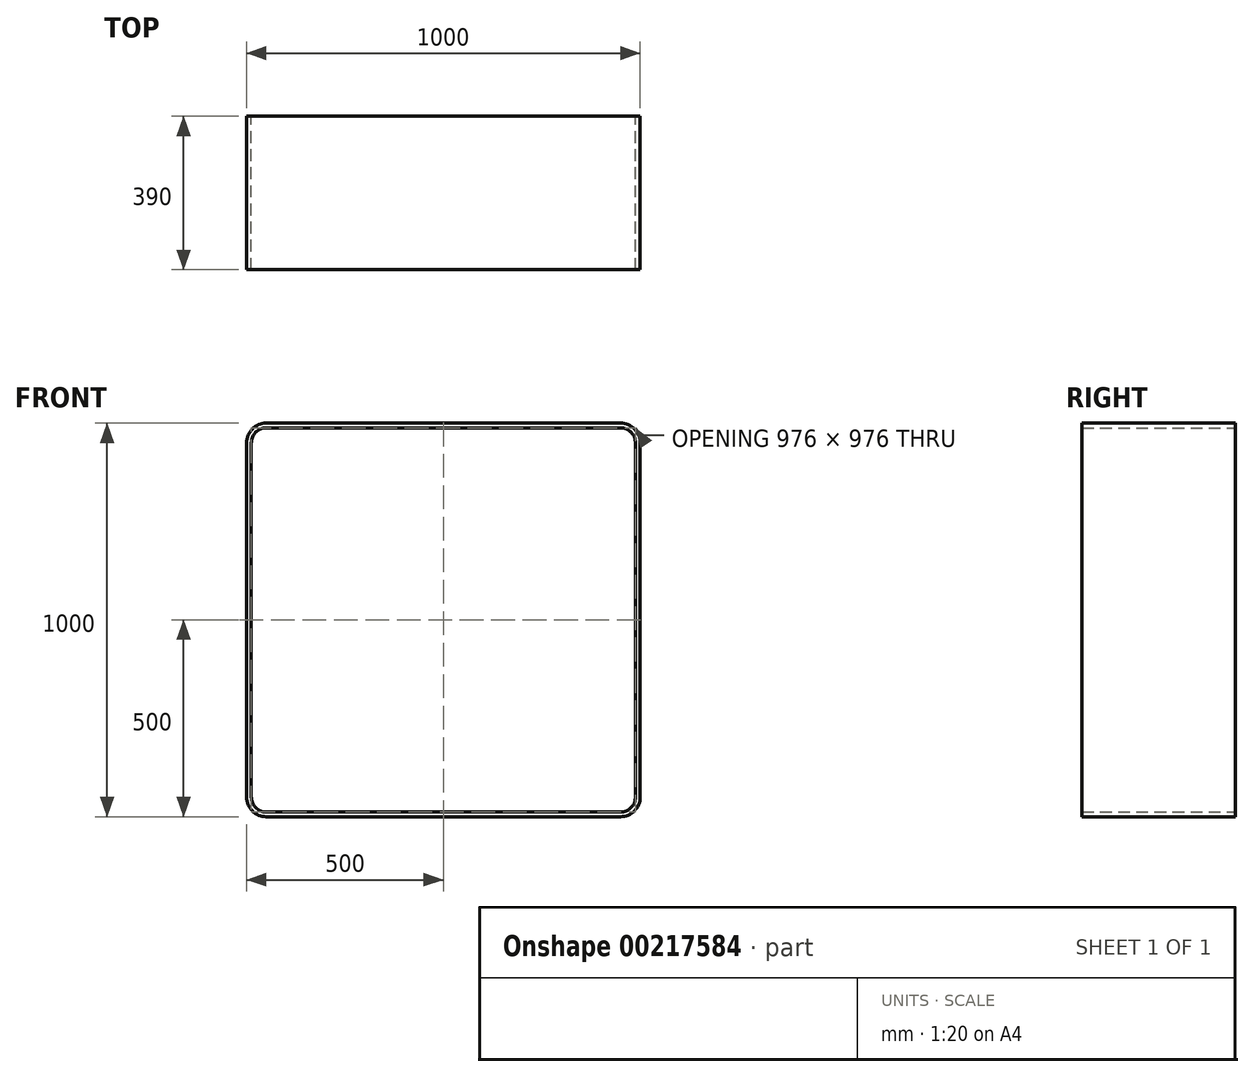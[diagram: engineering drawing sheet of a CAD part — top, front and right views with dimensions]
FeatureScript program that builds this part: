
annotation { "Feature Type Name" : "Feature", "Feature Type Description" : "" }
export const myFeature = defineFeature(function(context is Context, id is Id, definition is map)
    precondition{}
    {
        {
            var Q0;
            Q0=qCreatedBy(makeId("Front.planeOp"),FACE);
            var sketch = newSketch(context, id + "F0", { "sketchPlane" : qUnion([Q0])});
            skLineSegment(sketch, "E0.bottom", {"start": v(450, 500) * mm, "end": v(-450, 500) * mm});
            skLineSegment(sketch, "E0.top", {"start": v(450, -500) * mm, "end": v(-450, -500) * mm});
            skLineSegment(sketch, "E0.left", {"start": v(500, 450) * mm, "end": v(500, -450) * mm});
            skLineSegment(sketch, "E0.right", {"start": v(-500, 450) * mm, "end": v(-500, -450) * mm});
            skPoint(sketch, "E0.middle", {"position": v(0, 0) * mm});
            skPoint(sketch, "E1.visualSharp", {"position": v(-500, 500) * mm});
            skArc(sketch, "E1.filletArc", {"start": v(-450, 500) * mm, "mid": v(-485.36, 485.36) * mm, "end": v(-500, 450) * mm});
            skPoint(sketch, "E2.visualSharp", {"position": v(500, 500) * mm});
            skArc(sketch, "E2.filletArc", {"start": v(500, 450) * mm, "mid": v(485.36, 485.36) * mm, "end": v(450, 500) * mm});
            skPoint(sketch, "E3.visualSharp", {"position": v(500, -500) * mm});
            skArc(sketch, "E3.filletArc", {"start": v(450, -500) * mm, "mid": v(485.36, -485.36) * mm, "end": v(500, -450) * mm});
            skPoint(sketch, "E4.visualSharp", {"position": v(-500, -500) * mm});
            skArc(sketch, "E4.filletArc", {"start": v(-500, -450) * mm, "mid": v(-485.36, -485.36) * mm, "end": v(-450, -500) * mm});
            skLineSegment(sketch, "E5.0", {"start": v(450, 488) * mm, "end": v(-450, 488) * mm});
            skArc(sketch, "E5.1", {"start": v(488, 450) * mm, "mid": v(476.87, 476.87) * mm, "end": v(450, 488) * mm});
            skArc(sketch, "E5.2", {"start": v(-450, 488) * mm, "mid": v(-476.87, 476.87) * mm, "end": v(-488, 450) * mm});
            skLineSegment(sketch, "E5.3", {"start": v(488, 450) * mm, "end": v(488, -450) * mm});
            skLineSegment(sketch, "E5.4", {"start": v(-488, 450) * mm, "end": v(-488, -450) * mm});
            skArc(sketch, "E5.5", {"start": v(-488, -450) * mm, "mid": v(-476.87, -476.87) * mm, "end": v(-450, -488) * mm});
            skLineSegment(sketch, "E5.6", {"start": v(450, -488) * mm, "end": v(-450, -488) * mm});
            skArc(sketch, "E5.7", {"start": v(450, -488) * mm, "mid": v(476.87, -476.87) * mm, "end": v(488, -450) * mm});
            skSolve(sketch);
        }
        {
            var Q0;
            Q0 = qSketchRegion(id + "F0", true);
            extrude(context, id + "F1", {"entities" : qUnion([Q0]), "depth" : 390 * mm});
        }
    });
